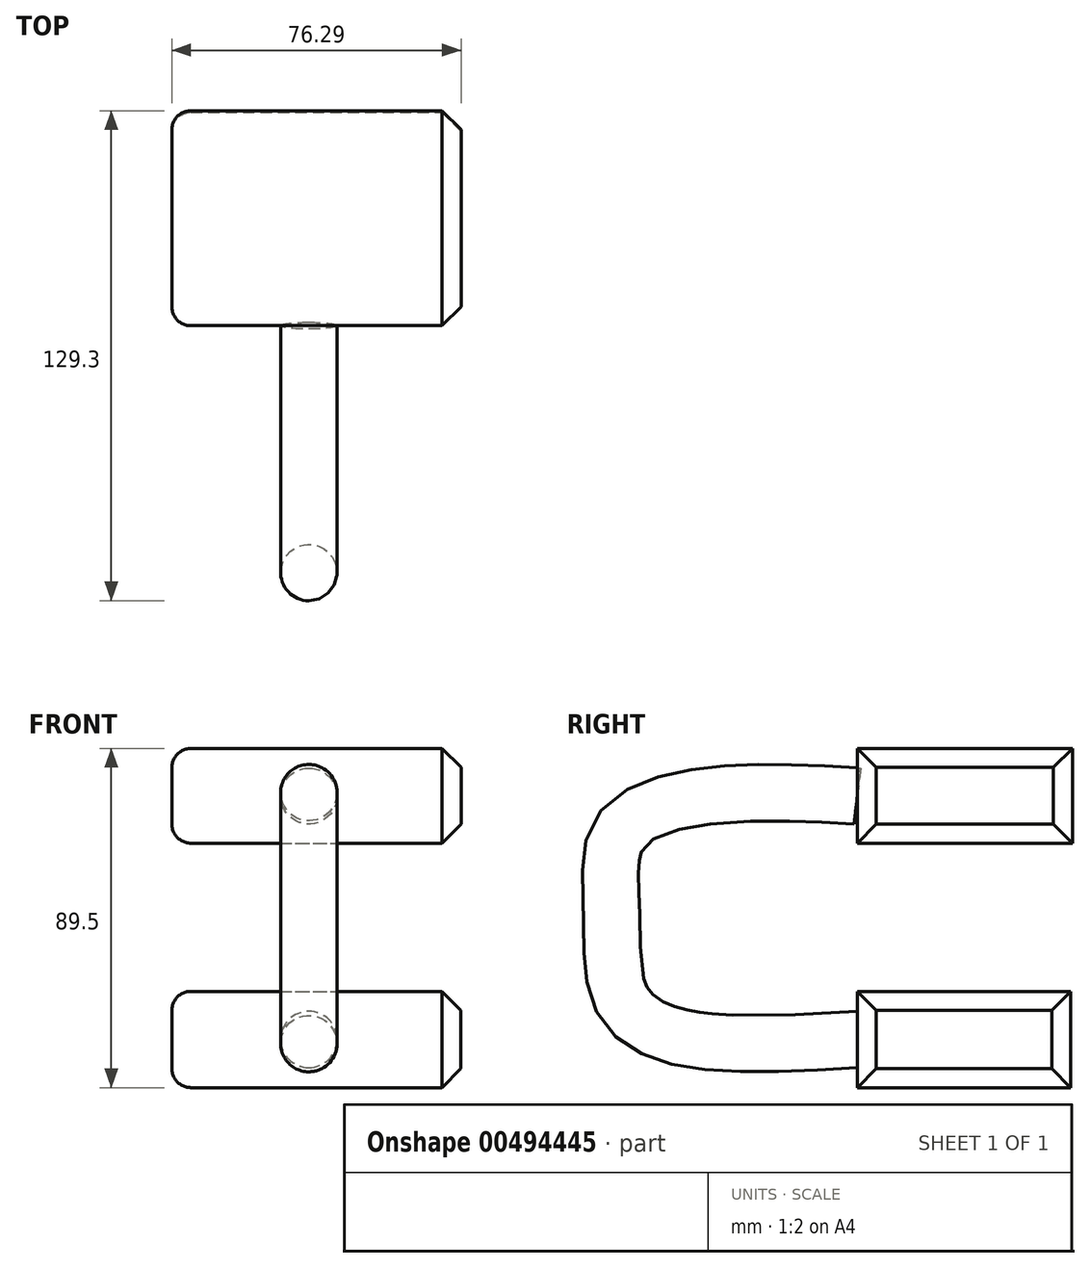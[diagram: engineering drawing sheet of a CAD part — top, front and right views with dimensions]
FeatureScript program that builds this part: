
annotation { "Feature Type Name" : "Feature", "Feature Type Description" : "" }
export const myFeature = defineFeature(function(context is Context, id is Id, definition is map)
    precondition{}
    {
        {
            var Q0;
            Q0=qCreatedBy(makeId("Top.planeOp"),FACE);
            var sketch = newSketch(context, id + "F0", { "sketchPlane" : qUnion([Q0])});
            skLineSegment(sketch, "E0.bottom", {"start": v(0, 0) * mm, "end": v(76.28, 0) * mm});
            skLineSegment(sketch, "E0.top", {"start": v(0, 56.3) * mm, "end": v(76.28, 56.3) * mm});
            skLineSegment(sketch, "E0.left", {"start": v(0, 0) * mm, "end": v(0, 56.3) * mm});
            skLineSegment(sketch, "E0.right", {"start": v(76.28, 0) * mm, "end": v(76.28, 56.3) * mm});
            skSolve(sketch);
        }
        {
            var Q0;
            Q0 = qSketchRegion(id + "F0", true);
            extrude(context, id + "F1", {"entities" : qUnion([Q0]), "depth" : 25.4 * mm});
        }
        {
            var Q0;
            Q0=makeQuery(id+"F1.opExtrude","SWEPT_FACE",FACE,{"disambiguationData":[OSD([sQuery(id+"F0.wireOp",EDGE,"E0.bottom")])]});
            var sketch = newSketch(context, id + "F2", { "sketchPlane" : qUnion([Q0])});
            skCircle(sketch, "E1", {"center": v(36.13, 12.71) * mm, "radius": 7.44 * mm});
            skSolve(sketch);
        }
        {
            var Q0;
            Q0=qCreatedBy(makeId("Right.planeOp"),FACE);
            cPlane(context, id + "F3", {"entities" : qUnion([Q0]), "cplaneType" : CPlaneType.OFFSET, "offset" : 36.1 * mm, "width" : 150 * mm, "height" : 150 * mm});
        }
        {
            var Q0;
            Q0=qCreatedBy(makeId("Top.planeOp"),FACE);
            cPlane(context, id + "F4", {"entities" : qUnion([Q0]), "cplaneType" : CPlaneType.OFFSET, "offset" : 64.5 * mm, "width" : 150 * mm, "height" : 150 * mm});
        }
        {
            var Q0;
            Q0=qCreatedBy(id+"F4.planeOp",FACE);
            var sketch = newSketch(context, id + "F5", { "sketchPlane" : qUnion([Q0])});
            skLineSegment(sketch, "E2.bottom", {"start": v(0, 56.73) * mm, "end": v(76.29, 56.73) * mm});
            skLineSegment(sketch, "E2.top", {"start": v(0, 0) * mm, "end": v(76.29, 0) * mm});
            skLineSegment(sketch, "E2.left", {"start": v(0, 56.73) * mm, "end": v(0, 0) * mm});
            skLineSegment(sketch, "E2.right", {"start": v(76.29, 56.73) * mm, "end": v(76.29, 0) * mm});
            skSolve(sketch);
        }
        {
            var Q0;
            Q0=makeQuery(id+"F5.imprint","IMPRINT",FACE,{"disambiguationData":[TD([[makeQuery(id+"F5.imprint","IMPRINT",EDGE,{"derivedFrom":sQuery(id+"F5.wireOp",EDGE,"E2.bottom")}),-1.0]])]});
            extrude(context, id + "F6", {"entities" : qUnion([Q0]), "depth" : 25 * mm});
        }
        {
            var Q0;
            Q0=qCreatedBy(id+"F3.planeOp",FACE);
            var sketch = newSketch(context, id + "F7", { "sketchPlane" : qUnion([Q0])});
            skFitSpline(sketch, "E3", {"points": [v(0, 12.78) * mm, v(-46.52, 13.33) * mm, v(-62.27, 23.6) * mm, v(-64.84, 47.28) * mm, v(-62.25, 67.88) * mm, v(-37.81, 77.1) * mm, v(0, 76.87) * mm], "startDerivative": vector(-241.93, -14.55) * mm, "endDerivative": vector(197.83, -11.8) * mm});
            skSolve(sketch);
        }
        {
            var Q0;
            Q0=makeQuery(id+"F2.imprint","IMPRINT",FACE,{"disambiguationData":[TD([[makeQuery(id+"F2.imprint","IMPRINT",EDGE,{"derivedFrom":sQuery(id+"F2.wireOp",EDGE,"E1")}),1.0]])]});
            var Q1;
            Q1=sQuery(id+"F7.wireOp",EDGE,"E3");
            sweep(context, id + "F8", {"profiles" : qUnion([Q0]), "path" : qUnion([Q1])});
        }
        {
            var Q0;
            Q0=makeQuery(id+"F1.opExtrude","SWEPT_EDGE",EDGE,{"disambiguationData":[OSD([sQuery(id+"F0.wireOp",EDGE,"E0.bottom"),sQuery(id+"F0.wireOp",EDGE,"E0.right")])]});
            var Q1;
            Q1=makeQuery(id+"F6.opExtrude","SWEPT_EDGE",EDGE,{"disambiguationData":[OSD([sQuery(id+"F5.wireOp",EDGE,"E2.top"),sQuery(id+"F5.wireOp",EDGE,"E2.right")])]});
            var Q2;
            Q2=makeQuery(id+"F1.opExtrude","SWEPT_EDGE",EDGE,{"disambiguationData":[OSD([sQuery(id+"F0.wireOp",EDGE,"E0.top"),sQuery(id+"F0.wireOp",EDGE,"E0.right")])]});
            var Q3;
            Q3=makeQuery(id+"F1.opExtrude","CAP_EDGE",EDGE,{"disambiguationData":[OSD([sQuery(id+"F0.wireOp",EDGE,"E0.right")])],"isStart":true});
            var Q4;
            Q4=makeQuery(id+"F1.opExtrude","CAP_EDGE",EDGE,{"disambiguationData":[OSD([sQuery(id+"F0.wireOp",EDGE,"E0.right")])],"isStart":false});
            var Q5;
            Q5=makeQuery(id+"F6.opExtrude","CAP_EDGE",EDGE,{"disambiguationData":[OSD([sQuery(id+"F5.wireOp",EDGE,"E2.right")])],"isStart":true});
            var Q6;
            Q6=makeQuery(id+"F6.opExtrude","CAP_EDGE",EDGE,{"disambiguationData":[OSD([sQuery(id+"F5.wireOp",EDGE,"E2.right")])],"isStart":false});
            var Q7;
            Q7=makeQuery(id+"F6.opExtrude","SWEPT_EDGE",EDGE,{"disambiguationData":[OSD([sQuery(id+"F5.wireOp",EDGE,"E2.bottom"),sQuery(id+"F5.wireOp",EDGE,"E2.right")])]});
            chamfer(context, id + "F9", {"entities" : qUnion([Q0, Q1, Q2, Q3, Q4, Q5, Q6, Q7]), "width" : 5 * mm, "tangentPropagation" : true});
        }
        {
            var Q0;
            Q0=makeQuery(id+"F6.opExtrude","CAP_EDGE",EDGE,{"disambiguationData":[OSD([sQuery(id+"F5.wireOp",EDGE,"E2.left")])],"isStart":false});
            var Q1;
            Q1=makeQuery(id+"F6.opExtrude","SWEPT_EDGE",EDGE,{"disambiguationData":[OSD([sQuery(id+"F5.wireOp",EDGE,"E2.top"),sQuery(id+"F5.wireOp",EDGE,"E2.left")])]});
            var Q2;
            Q2=makeQuery(id+"F6.opExtrude","CAP_EDGE",EDGE,{"disambiguationData":[OSD([sQuery(id+"F5.wireOp",EDGE,"E2.left")])],"isStart":true});
            var Q3;
            Q3=makeQuery(id+"F6.opExtrude","SWEPT_EDGE",EDGE,{"disambiguationData":[OSD([sQuery(id+"F5.wireOp",EDGE,"E2.bottom"),sQuery(id+"F5.wireOp",EDGE,"E2.left")])]});
            var Q4;
            Q4=makeQuery(id+"F1.opExtrude","SWEPT_EDGE",EDGE,{"disambiguationData":[OSD([sQuery(id+"F0.wireOp",EDGE,"E0.top"),sQuery(id+"F0.wireOp",EDGE,"E0.left")])]});
            var Q5;
            Q5=makeQuery(id+"F1.opExtrude","CAP_EDGE",EDGE,{"disambiguationData":[OSD([sQuery(id+"F0.wireOp",EDGE,"E0.left")])],"isStart":false});
            var Q6;
            Q6=makeQuery(id+"F1.opExtrude","CAP_EDGE",EDGE,{"disambiguationData":[OSD([sQuery(id+"F0.wireOp",EDGE,"E0.left")])],"isStart":true});
            var Q7;
            Q7=makeQuery(id+"F1.opExtrude","SWEPT_EDGE",EDGE,{"disambiguationData":[OSD([sQuery(id+"F0.wireOp",EDGE,"E0.bottom"),sQuery(id+"F0.wireOp",EDGE,"E0.left")])]});
            fillet(context, id + "F10", {"entities" : qUnion([Q0, Q1, Q2, Q3, Q4, Q5, Q6, Q7]), "radius" : 5 * mm, "tangentPropagation" : true, "allowEdgeOverflow" : false});
        }
    });
